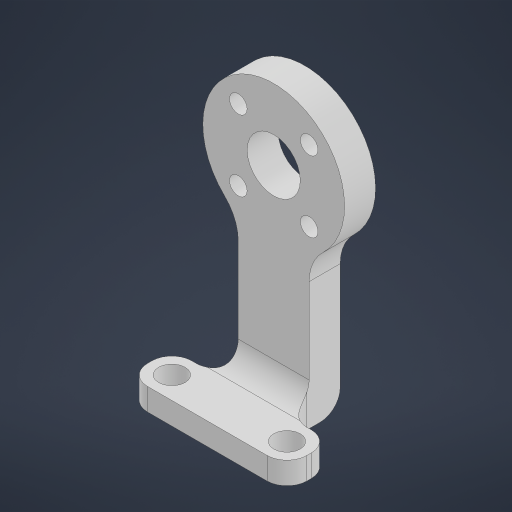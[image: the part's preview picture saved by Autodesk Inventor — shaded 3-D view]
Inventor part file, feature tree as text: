
AUTODESK INVENTOR PART (.ipt)
format: ipt  version: 2023.2 (Build 272271000, 271)  size: 276,992 bytes
history: native  units: mm
features: extrude x4, sketch x2, fillet x2, mirror x1
ambient origin geometry x8: Origin, YZ Plane, XZ Plane, XY Plane, X Axis, Y Axis, Z Axis, Center Point
bodies: Volumenkörper1 (feature_tree)
feature tree (9):
  sketch  "Skizze1"  dims[d0=25.0mm d1=25.0mm]
  extrude  "Extrusion1"  Depth=25.0mm
  extrude  "Extrusion2"  Depth=10.0mm
  extrude  "Extrusion3"  Depth=10.0mm
  extrude  "Extrusion4"  Depth=16.0mm
  mirror  "Spiegeln1"
  fillet  "Rundung1"  Radius=50.0mm
  fillet  "Rundung2"  Radius=47.5mm
  sketch  "Skizze2"  dims[d2=4.0mm d4=8.0mm d5=8.0mm d6=20.0mm d8=16.0mm d9=20.0mm d11=16.0mm d14=50.0mm d15=47.5mm d16=32.0mm d17=25.0mm d18=7.0mm d19=0.0mm d20=12.0mm d21=5.0mm d22=10.0mm d23=10.0mm d24=5.0mm d25=0.0mm d26=10.0mm d27=0.0mm d28=6.0mm d29=5.0mm d30=5.0mm d31=0.0mm d32=0.0mm d33=4.5mm d34=10.0mm]
